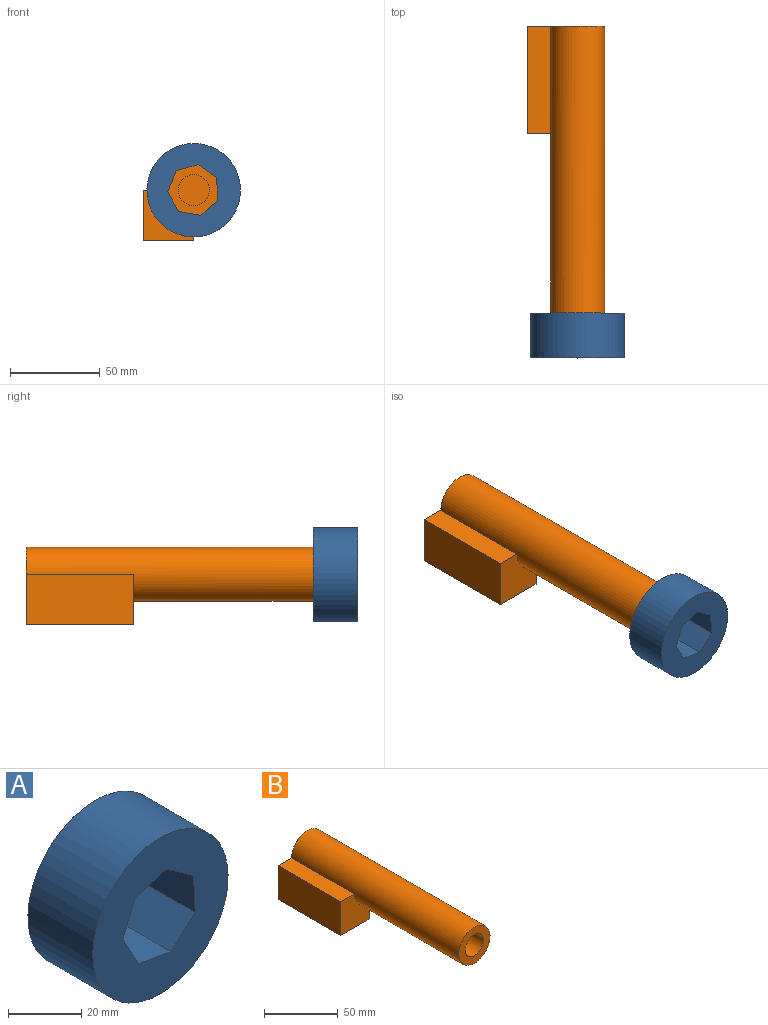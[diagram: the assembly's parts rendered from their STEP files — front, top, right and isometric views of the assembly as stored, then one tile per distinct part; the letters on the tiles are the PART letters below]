
ASSEMBLY  parts=2 mates=1
PART A: 10 faces, bbox 52.2x25x52.2 mm
  f0: plane 25x10.27mm, normal (-0.58,0,-0.81), area 315.4mm2, adj f1,f6,f8,f9
  f1: plane 25x12.6mm, normal (-1,0,-0.05), area 315.4mm2, adj f0,f2,f8,f9
  f2: plane 25x9.43mm, normal (-0.66,0,0.75), area 315.4mm2, adj f1,f3,f8,f9
  f3: plane 25x12.43mm, normal (0.17,0,0.99), area 315.4mm2, adj f2,f4,f8,f9
  f4: plane 25x11.06mm, normal (0.88,0,0.48), area 315.4mm2, adj f3,f5,f8,f9
  f5: plane 25x11.64mm, normal (0.92,0,-0.39), area 315.4mm2, adj f4,f6,f8,f9
  f6: plane 25x12.13mm, normal (0.27,0,-0.96), area 315.4mm2, adj f0,f5,f8,f9
  f7: cylinder r=26.08mm len=52.15mm, axis (0,1,0), area 4096mm2, adj f8,f9
  f8: plane 52.15x52.15mm, normal (0,-1,0), area 1557.8mm2, adj f0,f1,f2,f3,f4,f5,f6,f7
  f9: plane 52.15x52.15mm, normal (0,1,0), area 1557.8mm2, adj f0,f1,f2,f3,f4,f5,f6,f7
PART B: 10 faces, bbox 43x160x43 mm
  f0: cylinder r=15mm len=160mm, axis (0,1,0), area 13665.9mm2, adj f1,f2,f5,f6,f7
  f1: plane 30x30mm, normal (0,-1,0), area 469.8mm2, adj f0,f3
  f2: plane 43x43mm, normal (0,1,0), area 1314.1mm2, adj f0,f5,f6,f8,f9
  f3: cylinder r=8.69mm len=100mm, axis (0,-1,0), area 5458.3mm2, adj f1,f4
  f4: plane 17.37x17.37mm, normal (0,-1,0), area 237.1mm2, adj f3
  f5: plane 60x13mm, normal (1,0,0), area 780mm2, adj f0,f2,f7,f9
  f6: plane 60x13mm, normal (0,0,1), area 780mm2, adj f0,f2,f7,f8
  f7: plane 28x28mm, normal (0,-1,0), area 607.3mm2, adj f0,f5,f6,f8,f9
  f8: plane 60x28mm, normal (-1,0,0), area 1680mm2, adj f2,f6,f7,f9
  f9: plane 60x28mm, normal (0,0,-1), area 1680mm2, adj f2,f5,f7,f8
PLACE A at identity
PLACE B t=(0,160,4.01)mm
MATE revolute B.f3 <-> A.f7  axis (0,-1,0) through (0,0,4.01)mm
